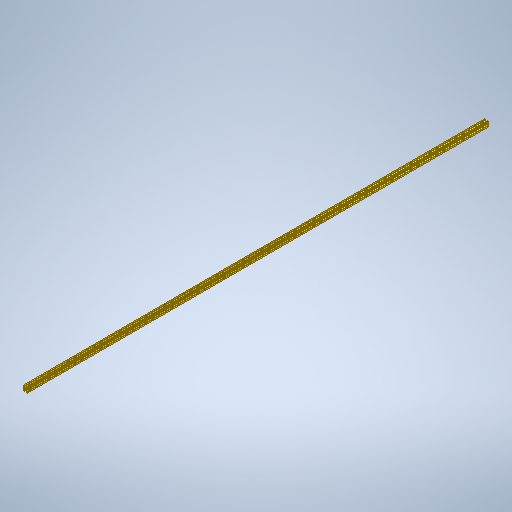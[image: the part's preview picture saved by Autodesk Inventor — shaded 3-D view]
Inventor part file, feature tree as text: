
AUTODESK INVENTOR PART (.ipt)
format: ipt  version: 2025.2 (Build 292293000, 293)  size: 359,424 bytes
history: native  units: mm
features: mirror x2, other x1, extrude x1, sketch x1
ambient origin geometry x8: Origin, YZ Plane, XZ Plane, XY Plane, X Axis, Y Axis, Z Axis, Center Point
bodies: Body1 (feature_tree)
feature tree (5):
  other  "Sólido1"
  extrude  "Extrusão1"  Depth=5.0mm
  mirror  "Espelhar1"
  mirror  "Espelhar2"
  sketch  "Esboço1"  dims[d0=20.0mm d2=5.0mm d3=6.0mm d5=2.0mm d7=1.0mm d8=6.0mm d9=1.0mm d10=0.5mm d11=0.5mm d12=0.5mm d14=0.5mm d15=0.5mm d16=10.0mm d17=2.5mm d18=2000.0mm d19=0.0mm d20=0.5mm d21=0.5mm]
